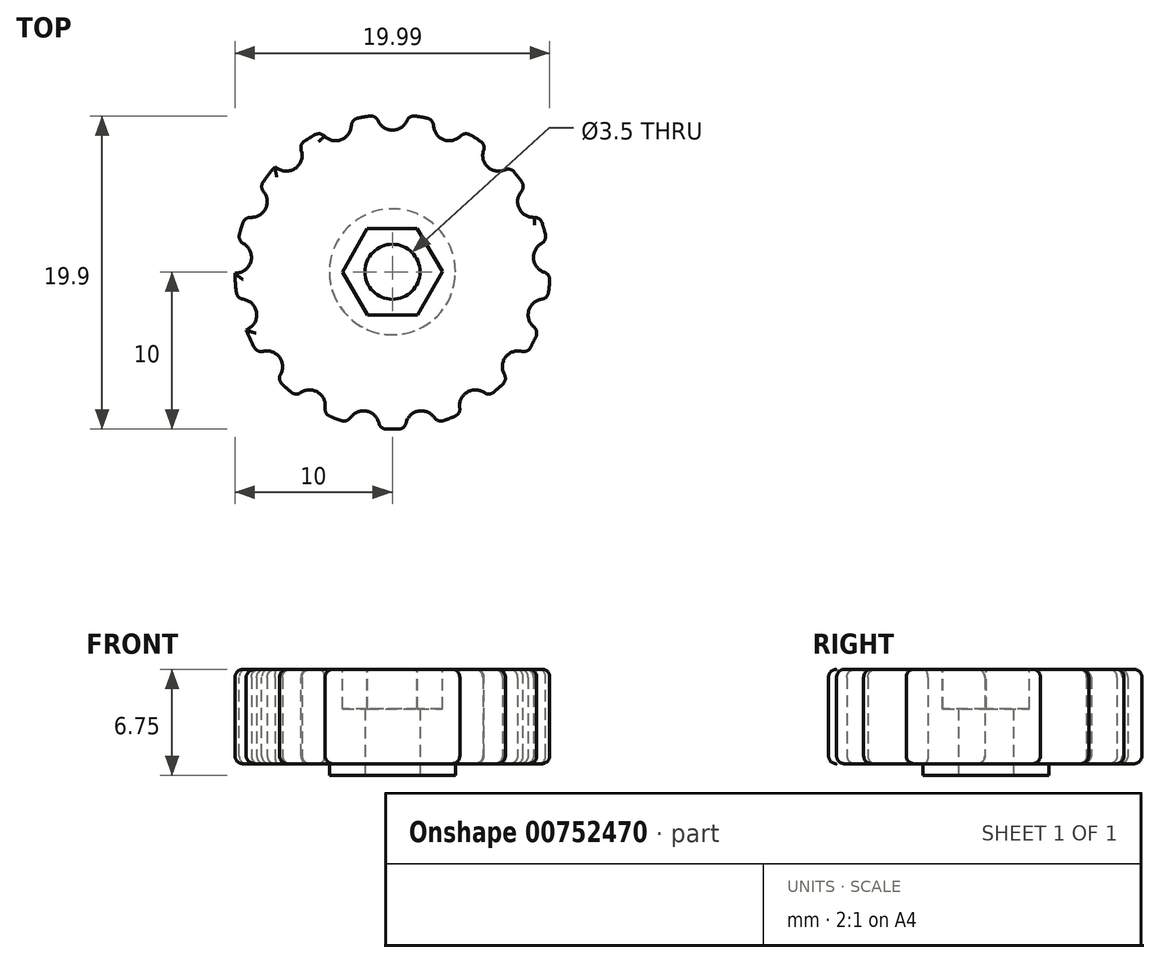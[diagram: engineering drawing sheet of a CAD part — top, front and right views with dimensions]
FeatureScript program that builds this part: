
annotation { "Feature Type Name" : "Feature", "Feature Type Description" : "" }
export const myFeature = defineFeature(function(context is Context, id is Id, definition is map)
    precondition{}
    {
        {
            var Q0;
            Q0=qCreatedBy(makeId("Top.planeOp"),FACE);
            var sketch = newSketch(context, id + "F0", { "sketchPlane" : qUnion([Q0])});
            skArc(sketch, "E0", {"start": v(-1, 9.95) * mm, "mid": v(-1.84, 9.83) * mm, "end": v(-2.66, 9.64) * mm});
            skArc(sketch, "E1", {"start": v(-1, 9.95) * mm, "mid": v(0, 9) * mm, "end": v(1, 9.95) * mm});
            skArc(sketch, "E2.1.0", {"start": v(-4.53, 8.92) * mm, "mid": v(-3.25, 8.4) * mm, "end": v(-2.66, 9.64) * mm});
            skArc(sketch, "E2.2.0", {"start": v(-7.44, 6.68) * mm, "mid": v(-6.06, 6.65) * mm, "end": v(-5.97, 8.03) * mm});
            skArc(sketch, "E3.2.3.0", {"start": v(-9.35, 3.54) * mm, "mid": v(-8.06, 4.01) * mm, "end": v(-8.46, 5.33) * mm});
            skArc(sketch, "E3.2.4.0", {"start": v(-10, -0.08) * mm, "mid": v(-8.96, 0.83) * mm, "end": v(-9.82, 1.91) * mm});
            skArc(sketch, "E3.2.5.0", {"start": v(-9.3, -3.68) * mm, "mid": v(-8.66, -2.46) * mm, "end": v(-9.84, -1.76) * mm});
            skArc(sketch, "E3.2.6.0", {"start": v(-7.34, -6.8) * mm, "mid": v(-7.18, -5.42) * mm, "end": v(-8.54, -5.2) * mm});
            skArc(sketch, "E3.2.7.0", {"start": v(-4.39, -8.99) * mm, "mid": v(-4.74, -7.65) * mm, "end": v(-6.09, -7.93) * mm});
            skArc(sketch, "E3.2.8.0", {"start": v(-0.85, -9.96) * mm, "mid": v(-1.65, -8.85) * mm, "end": v(-2.81, -9.6) * mm});
            skArc(sketch, "E3.2.9.0", {"start": v(2.81, -9.6) * mm, "mid": v(1.65, -8.85) * mm, "end": v(0.85, -9.96) * mm});
            skArc(sketch, "E3.2.10.0", {"start": v(6.09, -7.93) * mm, "mid": v(4.74, -7.65) * mm, "end": v(4.39, -8.99) * mm});
            skArc(sketch, "E3.2.11.0", {"start": v(8.54, -5.2) * mm, "mid": v(7.18, -5.42) * mm, "end": v(7.34, -6.8) * mm});
            skArc(sketch, "E3.2.12.0", {"start": v(9.84, -1.76) * mm, "mid": v(8.66, -2.46) * mm, "end": v(9.3, -3.68) * mm});
            skArc(sketch, "E3.2.13.0", {"start": v(9.82, 1.91) * mm, "mid": v(8.96, 0.83) * mm, "end": v(10, -0.08) * mm});
            skArc(sketch, "E3.2.14.0", {"start": v(8.46, 5.33) * mm, "mid": v(8.06, 4.01) * mm, "end": v(9.35, 3.54) * mm});
            skArc(sketch, "E3.2.15.0", {"start": v(5.97, 8.03) * mm, "mid": v(6.06, 6.65) * mm, "end": v(7.44, 6.68) * mm});
            skArc(sketch, "E4.2.16.0", {"start": v(2.66, 9.64) * mm, "mid": v(3.25, 8.4) * mm, "end": v(4.53, 8.92) * mm});
            skArc(sketch, "E5.trimOffspring", {"start": v(-4.53, 8.92) * mm, "mid": v(-5.26, 8.5) * mm, "end": v(-5.97, 8.03) * mm});
            skArc(sketch, "E6.trimOffspring", {"start": v(-7.44, 6.68) * mm, "mid": v(-7.98, 6.03) * mm, "end": v(-8.46, 5.33) * mm});
            skArc(sketch, "E7.trimOffspring", {"start": v(-9.35, 3.54) * mm, "mid": v(-9.62, 2.74) * mm, "end": v(-9.82, 1.91) * mm});
            skArc(sketch, "E8.trimOffspring", {"start": v(-10, -0.08) * mm, "mid": v(-9.96, -0.92) * mm, "end": v(-9.84, -1.76) * mm});
            skArc(sketch, "E9.trimOffspring", {"start": v(-9.3, -3.68) * mm, "mid": v(-8.95, -4.46) * mm, "end": v(-8.54, -5.2) * mm});
            skArc(sketch, "E10.trimOffspring", {"start": v(-7.34, -6.8) * mm, "mid": v(-6.74, -7.4) * mm, "end": v(-6.09, -7.93) * mm});
            skArc(sketch, "E11.trimOffspring", {"start": v(-4.39, -8.99) * mm, "mid": v(-3.61, -9.32) * mm, "end": v(-2.81, -9.6) * mm});
            skArc(sketch, "E12.trimOffspring", {"start": v(-0.85, -9.96) * mm, "mid": v(0, -10) * mm, "end": v(0.85, -9.96) * mm});
            skArc(sketch, "E13.trimOffspring", {"start": v(2.81, -9.6) * mm, "mid": v(3.61, -9.32) * mm, "end": v(4.39, -8.99) * mm});
            skArc(sketch, "E14.trimOffspring", {"start": v(6.09, -7.93) * mm, "mid": v(6.74, -7.4) * mm, "end": v(7.34, -6.8) * mm});
            skArc(sketch, "E15.trimOffspring", {"start": v(8.54, -5.2) * mm, "mid": v(8.95, -4.46) * mm, "end": v(9.3, -3.68) * mm});
            skArc(sketch, "E16.trimOffspring", {"start": v(9.84, -1.76) * mm, "mid": v(9.96, -0.92) * mm, "end": v(10, -0.08) * mm});
            skArc(sketch, "E17.trimOffspring", {"start": v(9.82, 1.91) * mm, "mid": v(9.62, 2.74) * mm, "end": v(9.35, 3.54) * mm});
            skArc(sketch, "E18.trimOffspring", {"start": v(8.46, 5.33) * mm, "mid": v(7.98, 6.03) * mm, "end": v(7.44, 6.68) * mm});
            skArc(sketch, "E19.trimOffspring", {"start": v(5.97, 8.03) * mm, "mid": v(5.26, 8.5) * mm, "end": v(4.53, 8.92) * mm});
            skArc(sketch, "E20.trimOffspring", {"start": v(2.66, 9.64) * mm, "mid": v(1.84, 9.83) * mm, "end": v(1, 9.95) * mm});
            skSolve(sketch);
        }
        {
            var Q0;
            Q0 = qSketchRegion(id + "F0", true);
            extrude(context, id + "F1", {"entities" : qUnion([Q0]), "depth" : 6 * mm, "offsetDistance" : 25 * mm});
        }
        {
            var Q0;
            Q0=makeQuery(id+"F1.opExtrude","SWEPT_EDGE",EDGE,{"disambiguationData":[OSD([sQuery(id+"F0.wireOp",EDGE,"E0"),sQuery(id+"F0.wireOp",EDGE,"E1")])]});
            var Q1;
            Q1=makeQuery(id+"F1.opExtrude","SWEPT_EDGE",EDGE,{"disambiguationData":[OSD([sQuery(id+"F0.wireOp",EDGE,"E4.2.16.0"),sQuery(id+"F0.wireOp",EDGE,"E20.trimOffspring")])]});
            var Q2;
            Q2=makeQuery(id+"F1.opExtrude","SWEPT_EDGE",EDGE,{"disambiguationData":[OSD([sQuery(id+"F0.wireOp",EDGE,"E1"),sQuery(id+"F0.wireOp",EDGE,"E20.trimOffspring")])]});
            var Q3;
            Q3=makeQuery(id+"F1.opExtrude","SWEPT_EDGE",EDGE,{"disambiguationData":[OSD([sQuery(id+"F0.wireOp",EDGE,"E4.2.16.0"),sQuery(id+"F0.wireOp",EDGE,"E19.trimOffspring")])]});
            var Q4;
            Q4=makeQuery(id+"F1.opExtrude","SWEPT_EDGE",EDGE,{"disambiguationData":[OSD([sQuery(id+"F0.wireOp",EDGE,"E3.2.15.0"),sQuery(id+"F0.wireOp",EDGE,"E19.trimOffspring")])]});
            var Q5;
            Q5=makeQuery(id+"F1.opExtrude","SWEPT_EDGE",EDGE,{"disambiguationData":[OSD([sQuery(id+"F0.wireOp",EDGE,"E3.2.15.0"),sQuery(id+"F0.wireOp",EDGE,"E18.trimOffspring")])]});
            var Q6;
            Q6=makeQuery(id+"F1.opExtrude","SWEPT_EDGE",EDGE,{"disambiguationData":[OSD([sQuery(id+"F0.wireOp",EDGE,"E3.2.14.0"),sQuery(id+"F0.wireOp",EDGE,"E18.trimOffspring")])]});
            var Q7;
            Q7=makeQuery(id+"F1.opExtrude","SWEPT_EDGE",EDGE,{"disambiguationData":[OSD([sQuery(id+"F0.wireOp",EDGE,"E3.2.14.0"),sQuery(id+"F0.wireOp",EDGE,"E17.trimOffspring")])]});
            var Q8;
            Q8=makeQuery(id+"F1.opExtrude","SWEPT_EDGE",EDGE,{"disambiguationData":[OSD([sQuery(id+"F0.wireOp",EDGE,"E3.2.13.0"),sQuery(id+"F0.wireOp",EDGE,"E17.trimOffspring")])]});
            var Q9;
            Q9=makeQuery(id+"F1.opExtrude","SWEPT_EDGE",EDGE,{"disambiguationData":[OSD([sQuery(id+"F0.wireOp",EDGE,"E3.2.13.0"),sQuery(id+"F0.wireOp",EDGE,"E16.trimOffspring")])]});
            var Q10;
            Q10=makeQuery(id+"F1.opExtrude","SWEPT_EDGE",EDGE,{"disambiguationData":[OSD([sQuery(id+"F0.wireOp",EDGE,"E3.2.12.0"),sQuery(id+"F0.wireOp",EDGE,"E16.trimOffspring")])]});
            var Q11;
            Q11=makeQuery(id+"F1.opExtrude","SWEPT_EDGE",EDGE,{"disambiguationData":[OSD([sQuery(id+"F0.wireOp",EDGE,"E3.2.12.0"),sQuery(id+"F0.wireOp",EDGE,"E15.trimOffspring")])]});
            var Q12;
            Q12=makeQuery(id+"F1.opExtrude","SWEPT_EDGE",EDGE,{"disambiguationData":[OSD([sQuery(id+"F0.wireOp",EDGE,"E3.2.11.0"),sQuery(id+"F0.wireOp",EDGE,"E15.trimOffspring")])]});
            var Q13;
            Q13=makeQuery(id+"F1.opExtrude","SWEPT_EDGE",EDGE,{"disambiguationData":[OSD([sQuery(id+"F0.wireOp",EDGE,"E3.2.11.0"),sQuery(id+"F0.wireOp",EDGE,"E14.trimOffspring")])]});
            var Q14;
            Q14=makeQuery(id+"F1.opExtrude","SWEPT_EDGE",EDGE,{"disambiguationData":[OSD([sQuery(id+"F0.wireOp",EDGE,"E3.2.10.0"),sQuery(id+"F0.wireOp",EDGE,"E14.trimOffspring")])]});
            var Q15;
            Q15=makeQuery(id+"F1.opExtrude","SWEPT_EDGE",EDGE,{"disambiguationData":[OSD([sQuery(id+"F0.wireOp",EDGE,"E3.2.10.0"),sQuery(id+"F0.wireOp",EDGE,"E13.trimOffspring")])]});
            var Q16;
            Q16=makeQuery(id+"F1.opExtrude","SWEPT_EDGE",EDGE,{"disambiguationData":[OSD([sQuery(id+"F0.wireOp",EDGE,"E3.2.9.0"),sQuery(id+"F0.wireOp",EDGE,"E13.trimOffspring")])]});
            var Q17;
            Q17=makeQuery(id+"F1.opExtrude","SWEPT_EDGE",EDGE,{"disambiguationData":[OSD([sQuery(id+"F0.wireOp",EDGE,"E3.2.9.0"),sQuery(id+"F0.wireOp",EDGE,"E12.trimOffspring")])]});
            var Q18;
            Q18=makeQuery(id+"F1.opExtrude","SWEPT_EDGE",EDGE,{"disambiguationData":[OSD([sQuery(id+"F0.wireOp",EDGE,"E3.2.8.0"),sQuery(id+"F0.wireOp",EDGE,"E12.trimOffspring")])]});
            var Q19;
            Q19=makeQuery(id+"F1.opExtrude","SWEPT_EDGE",EDGE,{"disambiguationData":[OSD([sQuery(id+"F0.wireOp",EDGE,"E3.2.8.0"),sQuery(id+"F0.wireOp",EDGE,"E11.trimOffspring")])]});
            var Q20;
            Q20=makeQuery(id+"F1.opExtrude","SWEPT_EDGE",EDGE,{"disambiguationData":[OSD([sQuery(id+"F0.wireOp",EDGE,"E3.2.7.0"),sQuery(id+"F0.wireOp",EDGE,"E11.trimOffspring")])]});
            var Q21;
            Q21=makeQuery(id+"F1.opExtrude","SWEPT_EDGE",EDGE,{"disambiguationData":[OSD([sQuery(id+"F0.wireOp",EDGE,"E3.2.7.0"),sQuery(id+"F0.wireOp",EDGE,"E10.trimOffspring")])]});
            var Q22;
            Q22=makeQuery(id+"F1.opExtrude","SWEPT_EDGE",EDGE,{"disambiguationData":[OSD([sQuery(id+"F0.wireOp",EDGE,"E3.2.6.0"),sQuery(id+"F0.wireOp",EDGE,"E10.trimOffspring")])]});
            var Q23;
            Q23=makeQuery(id+"F1.opExtrude","SWEPT_EDGE",EDGE,{"disambiguationData":[OSD([sQuery(id+"F0.wireOp",EDGE,"E3.2.6.0"),sQuery(id+"F0.wireOp",EDGE,"E9.trimOffspring")])]});
            var Q24;
            Q24=makeQuery(id+"F1.opExtrude","SWEPT_EDGE",EDGE,{"disambiguationData":[OSD([sQuery(id+"F0.wireOp",EDGE,"E3.2.5.0"),sQuery(id+"F0.wireOp",EDGE,"E8.trimOffspring")])]});
            var Q25;
            Q25=makeQuery(id+"F1.opExtrude","SWEPT_EDGE",EDGE,{"disambiguationData":[OSD([sQuery(id+"F0.wireOp",EDGE,"E3.2.4.0"),sQuery(id+"F0.wireOp",EDGE,"E7.trimOffspring")])]});
            var Q26;
            Q26=makeQuery(id+"F1.opExtrude","SWEPT_EDGE",EDGE,{"disambiguationData":[OSD([sQuery(id+"F0.wireOp",EDGE,"E3.2.3.0"),sQuery(id+"F0.wireOp",EDGE,"E7.trimOffspring")])]});
            var Q27;
            Q27=makeQuery(id+"F1.opExtrude","SWEPT_EDGE",EDGE,{"disambiguationData":[OSD([sQuery(id+"F0.wireOp",EDGE,"E3.2.3.0"),sQuery(id+"F0.wireOp",EDGE,"E6.trimOffspring")])]});
            var Q28;
            Q28=makeQuery(id+"F1.opExtrude","SWEPT_EDGE",EDGE,{"disambiguationData":[OSD([sQuery(id+"F0.wireOp",EDGE,"E2.2.0"),sQuery(id+"F0.wireOp",EDGE,"E5.trimOffspring")])]});
            var Q29;
            Q29=makeQuery(id+"F1.opExtrude","SWEPT_EDGE",EDGE,{"disambiguationData":[OSD([sQuery(id+"F0.wireOp",EDGE,"E2.1.0"),sQuery(id+"F0.wireOp",EDGE,"E5.trimOffspring")])]});
            var Q30;
            Q30=makeQuery(id+"F1.opExtrude","SWEPT_EDGE",EDGE,{"disambiguationData":[OSD([sQuery(id+"F0.wireOp",EDGE,"E0"),sQuery(id+"F0.wireOp",EDGE,"E2.1.0")])]});
            var Q31;
            Q31=makeQuery(id+"F1.opExtrude","CAP_FACE",FACE,{"disambiguationData":[OSD([sQuery(id+"F0.wireOp",EDGE,"E0"),sQuery(id+"F0.wireOp",EDGE,"E1"),sQuery(id+"F0.wireOp",EDGE,"E2.1.0"),sQuery(id+"F0.wireOp",EDGE,"E2.2.0"),sQuery(id+"F0.wireOp",EDGE,"E3.2.3.0"),sQuery(id+"F0.wireOp",EDGE,"E3.2.4.0"),sQuery(id+"F0.wireOp",EDGE,"E3.2.5.0"),sQuery(id+"F0.wireOp",EDGE,"E3.2.6.0"),sQuery(id+"F0.wireOp",EDGE,"E3.2.7.0"),sQuery(id+"F0.wireOp",EDGE,"E3.2.8.0"),sQuery(id+"F0.wireOp",EDGE,"E3.2.9.0"),sQuery(id+"F0.wireOp",EDGE,"E3.2.10.0"),sQuery(id+"F0.wireOp",EDGE,"E3.2.11.0"),sQuery(id+"F0.wireOp",EDGE,"E3.2.12.0"),sQuery(id+"F0.wireOp",EDGE,"E3.2.13.0"),sQuery(id+"F0.wireOp",EDGE,"E3.2.14.0"),sQuery(id+"F0.wireOp",EDGE,"E3.2.15.0"),sQuery(id+"F0.wireOp",EDGE,"E4.2.16.0"),sQuery(id+"F0.wireOp",EDGE,"E5.trimOffspring"),sQuery(id+"F0.wireOp",EDGE,"E6.trimOffspring"),sQuery(id+"F0.wireOp",EDGE,"E7.trimOffspring"),sQuery(id+"F0.wireOp",EDGE,"E8.trimOffspring"),sQuery(id+"F0.wireOp",EDGE,"E9.trimOffspring"),sQuery(id+"F0.wireOp",EDGE,"E10.trimOffspring"),sQuery(id+"F0.wireOp",EDGE,"E11.trimOffspring"),sQuery(id+"F0.wireOp",EDGE,"E12.trimOffspring"),sQuery(id+"F0.wireOp",EDGE,"E13.trimOffspring"),sQuery(id+"F0.wireOp",EDGE,"E14.trimOffspring"),sQuery(id+"F0.wireOp",EDGE,"E15.trimOffspring"),sQuery(id+"F0.wireOp",EDGE,"E16.trimOffspring"),sQuery(id+"F0.wireOp",EDGE,"E17.trimOffspring"),sQuery(id+"F0.wireOp",EDGE,"E18.trimOffspring"),sQuery(id+"F0.wireOp",EDGE,"E19.trimOffspring"),sQuery(id+"F0.wireOp",EDGE,"E20.trimOffspring")])],"isStart":false});
            var Q32;
            Q32=makeQuery(id+"F1.opExtrude","CAP_FACE",FACE,{"disambiguationData":[OSD([sQuery(id+"F0.wireOp",EDGE,"E0"),sQuery(id+"F0.wireOp",EDGE,"E1"),sQuery(id+"F0.wireOp",EDGE,"E2.1.0"),sQuery(id+"F0.wireOp",EDGE,"E2.2.0"),sQuery(id+"F0.wireOp",EDGE,"E3.2.3.0"),sQuery(id+"F0.wireOp",EDGE,"E3.2.4.0"),sQuery(id+"F0.wireOp",EDGE,"E3.2.5.0"),sQuery(id+"F0.wireOp",EDGE,"E3.2.6.0"),sQuery(id+"F0.wireOp",EDGE,"E3.2.7.0"),sQuery(id+"F0.wireOp",EDGE,"E3.2.8.0"),sQuery(id+"F0.wireOp",EDGE,"E3.2.9.0"),sQuery(id+"F0.wireOp",EDGE,"E3.2.10.0"),sQuery(id+"F0.wireOp",EDGE,"E3.2.11.0"),sQuery(id+"F0.wireOp",EDGE,"E3.2.12.0"),sQuery(id+"F0.wireOp",EDGE,"E3.2.13.0"),sQuery(id+"F0.wireOp",EDGE,"E3.2.14.0"),sQuery(id+"F0.wireOp",EDGE,"E3.2.15.0"),sQuery(id+"F0.wireOp",EDGE,"E4.2.16.0"),sQuery(id+"F0.wireOp",EDGE,"E5.trimOffspring"),sQuery(id+"F0.wireOp",EDGE,"E6.trimOffspring"),sQuery(id+"F0.wireOp",EDGE,"E7.trimOffspring"),sQuery(id+"F0.wireOp",EDGE,"E8.trimOffspring"),sQuery(id+"F0.wireOp",EDGE,"E9.trimOffspring"),sQuery(id+"F0.wireOp",EDGE,"E10.trimOffspring"),sQuery(id+"F0.wireOp",EDGE,"E11.trimOffspring"),sQuery(id+"F0.wireOp",EDGE,"E12.trimOffspring"),sQuery(id+"F0.wireOp",EDGE,"E13.trimOffspring"),sQuery(id+"F0.wireOp",EDGE,"E14.trimOffspring"),sQuery(id+"F0.wireOp",EDGE,"E15.trimOffspring"),sQuery(id+"F0.wireOp",EDGE,"E16.trimOffspring"),sQuery(id+"F0.wireOp",EDGE,"E17.trimOffspring"),sQuery(id+"F0.wireOp",EDGE,"E18.trimOffspring"),sQuery(id+"F0.wireOp",EDGE,"E19.trimOffspring"),sQuery(id+"F0.wireOp",EDGE,"E20.trimOffspring")])],"isStart":true});
            fillet(context, id + "F2", {"entities" : qUnion([Q0, Q1, Q2, Q3, Q4, Q5, Q6, Q7, Q8, Q9, Q10, Q11, Q12, Q13, Q14, Q15, Q16, Q17, Q18, Q19, Q20, Q21, Q22, Q23, Q24, Q25, Q26, Q27, Q28, Q29, Q30, Q31, Q32]), "radius" : .5 * mm, "tangentPropagation" : true, "allowEdgeOverflow" : false});
        }
        {
            var Q0;
            Q0=makeQuery(id+"F1.opExtrude","CAP_FACE",FACE,{"disambiguationData":[OSD([sQuery(id+"F0.wireOp",EDGE,"E0"),sQuery(id+"F0.wireOp",EDGE,"E1"),sQuery(id+"F0.wireOp",EDGE,"E2.1.0"),sQuery(id+"F0.wireOp",EDGE,"E2.2.0"),sQuery(id+"F0.wireOp",EDGE,"E3.2.3.0"),sQuery(id+"F0.wireOp",EDGE,"E3.2.4.0"),sQuery(id+"F0.wireOp",EDGE,"E3.2.5.0"),sQuery(id+"F0.wireOp",EDGE,"E3.2.6.0"),sQuery(id+"F0.wireOp",EDGE,"E3.2.7.0"),sQuery(id+"F0.wireOp",EDGE,"E3.2.8.0"),sQuery(id+"F0.wireOp",EDGE,"E3.2.9.0"),sQuery(id+"F0.wireOp",EDGE,"E3.2.10.0"),sQuery(id+"F0.wireOp",EDGE,"E3.2.11.0"),sQuery(id+"F0.wireOp",EDGE,"E3.2.12.0"),sQuery(id+"F0.wireOp",EDGE,"E3.2.13.0"),sQuery(id+"F0.wireOp",EDGE,"E3.2.14.0"),sQuery(id+"F0.wireOp",EDGE,"E3.2.15.0"),sQuery(id+"F0.wireOp",EDGE,"E4.2.16.0"),sQuery(id+"F0.wireOp",EDGE,"E5.trimOffspring"),sQuery(id+"F0.wireOp",EDGE,"E6.trimOffspring"),sQuery(id+"F0.wireOp",EDGE,"E7.trimOffspring"),sQuery(id+"F0.wireOp",EDGE,"E8.trimOffspring"),sQuery(id+"F0.wireOp",EDGE,"E9.trimOffspring"),sQuery(id+"F0.wireOp",EDGE,"E10.trimOffspring"),sQuery(id+"F0.wireOp",EDGE,"E11.trimOffspring"),sQuery(id+"F0.wireOp",EDGE,"E12.trimOffspring"),sQuery(id+"F0.wireOp",EDGE,"E13.trimOffspring"),sQuery(id+"F0.wireOp",EDGE,"E14.trimOffspring"),sQuery(id+"F0.wireOp",EDGE,"E15.trimOffspring"),sQuery(id+"F0.wireOp",EDGE,"E16.trimOffspring"),sQuery(id+"F0.wireOp",EDGE,"E17.trimOffspring"),sQuery(id+"F0.wireOp",EDGE,"E18.trimOffspring"),sQuery(id+"F0.wireOp",EDGE,"E19.trimOffspring"),sQuery(id+"F0.wireOp",EDGE,"E20.trimOffspring")])],"isStart":false});
            var sketch = newSketch(context, id + "F3", { "sketchPlane" : qUnion([Q0])});
            skCircle(sketch, "E21.cCircle", {"center": v(0, 0) * mm, "radius": 2.75 * mm, "construction": true});
            skLineSegment(sketch, "E21.0", {"start": v(3.18, 0.01) * mm, "end": v(1.6, -2.74) * mm});
            skLineSegment(sketch, "E21.1", {"start": v(1.6, -2.74) * mm, "end": v(-1.58, -2.76) * mm});
            skLineSegment(sketch, "E21.2", {"start": v(-1.58, -2.76) * mm, "end": v(-3.18, -0.01) * mm});
            skLineSegment(sketch, "E21.3", {"start": v(-3.18, -0.01) * mm, "end": v(-1.6, 2.74) * mm});
            skLineSegment(sketch, "E21.4", {"start": v(-1.6, 2.74) * mm, "end": v(1.58, 2.76) * mm});
            skLineSegment(sketch, "E21.5", {"start": v(1.58, 2.76) * mm, "end": v(3.18, 0.01) * mm});
            skPoint(sketch, "E21.0.midPoint", {"position": v(2.39, -1.37) * mm});
            skSolve(sketch);
        }
        {
            var Q0;
            Q0=makeQuery(id+"F3.imprint","IMPRINT",FACE,{"disambiguationData":[TD([[makeQuery(id+"F3.imprint","IMPRINT",EDGE,{"derivedFrom":sQuery(id+"F3.wireOp",EDGE,"E21.0")}),-1.0]])]});
            extrude(context, id + "F4", {"entities" : qUnion([Q0]), "operationType" : NewBodyOperationType.REMOVE, "oppositeDirection" : true, "depth" : 2.5 * mm, "offsetDistance" : 25 * mm});
        }
        {
            var Q0;
            Q0=makeQuery(id+"F1.opExtrude","CAP_FACE",FACE,{"disambiguationData":[OSD([sQuery(id+"F0.wireOp",EDGE,"E0"),sQuery(id+"F0.wireOp",EDGE,"E1"),sQuery(id+"F0.wireOp",EDGE,"E2.1.0"),sQuery(id+"F0.wireOp",EDGE,"E2.2.0"),sQuery(id+"F0.wireOp",EDGE,"E3.2.3.0"),sQuery(id+"F0.wireOp",EDGE,"E3.2.4.0"),sQuery(id+"F0.wireOp",EDGE,"E3.2.5.0"),sQuery(id+"F0.wireOp",EDGE,"E3.2.6.0"),sQuery(id+"F0.wireOp",EDGE,"E3.2.7.0"),sQuery(id+"F0.wireOp",EDGE,"E3.2.8.0"),sQuery(id+"F0.wireOp",EDGE,"E3.2.9.0"),sQuery(id+"F0.wireOp",EDGE,"E3.2.10.0"),sQuery(id+"F0.wireOp",EDGE,"E3.2.11.0"),sQuery(id+"F0.wireOp",EDGE,"E3.2.12.0"),sQuery(id+"F0.wireOp",EDGE,"E3.2.13.0"),sQuery(id+"F0.wireOp",EDGE,"E3.2.14.0"),sQuery(id+"F0.wireOp",EDGE,"E3.2.15.0"),sQuery(id+"F0.wireOp",EDGE,"E4.2.16.0"),sQuery(id+"F0.wireOp",EDGE,"E5.trimOffspring"),sQuery(id+"F0.wireOp",EDGE,"E6.trimOffspring"),sQuery(id+"F0.wireOp",EDGE,"E7.trimOffspring"),sQuery(id+"F0.wireOp",EDGE,"E8.trimOffspring"),sQuery(id+"F0.wireOp",EDGE,"E9.trimOffspring"),sQuery(id+"F0.wireOp",EDGE,"E10.trimOffspring"),sQuery(id+"F0.wireOp",EDGE,"E11.trimOffspring"),sQuery(id+"F0.wireOp",EDGE,"E12.trimOffspring"),sQuery(id+"F0.wireOp",EDGE,"E13.trimOffspring"),sQuery(id+"F0.wireOp",EDGE,"E14.trimOffspring"),sQuery(id+"F0.wireOp",EDGE,"E15.trimOffspring"),sQuery(id+"F0.wireOp",EDGE,"E16.trimOffspring"),sQuery(id+"F0.wireOp",EDGE,"E17.trimOffspring"),sQuery(id+"F0.wireOp",EDGE,"E18.trimOffspring"),sQuery(id+"F0.wireOp",EDGE,"E19.trimOffspring"),sQuery(id+"F0.wireOp",EDGE,"E20.trimOffspring")])],"isStart":true});
            var sketch = newSketch(context, id + "F5", { "sketchPlane" : qUnion([Q0])});
            skCircle(sketch, "E22", {"center": v(0, 0) * mm, "radius": 4 * mm});
            skSolve(sketch);
        }
        {
            var Q0;
            Q0 = qSketchRegion(id + "F5", true);
            extrude(context, id + "F6", {"entities" : qUnion([Q0]), "operationType" : NewBodyOperationType.ADD, "depth" : .75 * mm, "offsetDistance" : 25 * mm});
        }
        {
            var Q0;
            Q0=makeQuery(id+"F6.opExtrude","CAP_FACE",FACE,{"disambiguationData":[OSD([sQuery(id+"F5.wireOp",EDGE,"E22")])],"isStart":false});
            var sketch = newSketch(context, id + "F7", { "sketchPlane" : qUnion([Q0])});
            skCircle(sketch, "E23", {"center": v(0, 0) * mm, "radius": 1.75 * mm});
            skSolve(sketch);
        }
        {
            var Q0;
            Q0=makeQuery(id+"F7.imprint","IMPRINT",FACE,{"disambiguationData":[TD([[makeQuery(id+"F7.imprint","IMPRINT",EDGE,{"derivedFrom":sQuery(id+"F7.wireOp",EDGE,"E23")}),1.0]])]});
            extrude(context, id + "F8", {"entities" : qUnion([Q0]), "operationType" : NewBodyOperationType.REMOVE, "oppositeDirection" : true, "depth" : (6) * mm, "offsetDistance" : 25 * mm});
        }
    });
